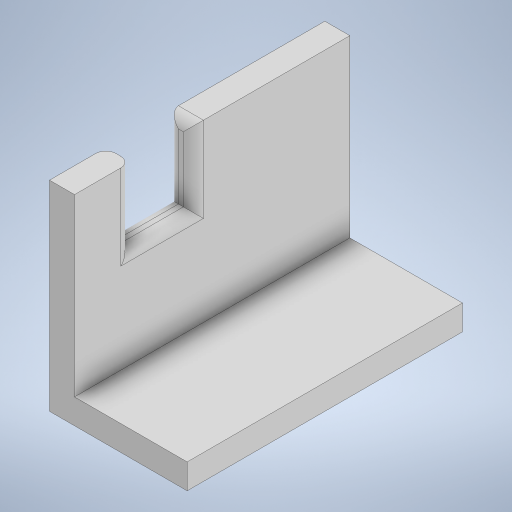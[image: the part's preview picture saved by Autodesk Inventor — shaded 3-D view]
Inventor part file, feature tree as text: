
AUTODESK INVENTOR PART (.ipt)
format: ipt  version: 2023 (Build 270158000, 158)  size: 224,768 bytes
history: native  units: in
note: dims shown in document units (in); Inventor stores cm internally (conversion verified against a paired STEP export)
features: extrude x2, sketch x2, fillet x1
ambient origin geometry x8: Origin, YZ Plane, XZ Plane, XY Plane, X Axis, Y Axis, Z Axis, Center Point
bodies: Solid1 (feature_tree)
feature tree (5):
  extrude  "Extrusion1"  Depth=0.6299in
  extrude  "Extrusion3"  Depth=0.8661in TaperAngle=0.0deg
  fillet  "Fillet1"  Radius=0.1969in
  sketch  "Sketch1"  dims[d0=0.0787in d1=0.6299in]
  sketch  "Sketch3"  dims[d2=0.3543in d3=0.8661in d4=0.0in d9=0.1969in d10=0.2362in d11=0.3937in d12=0.0in d13=0.0315in]
